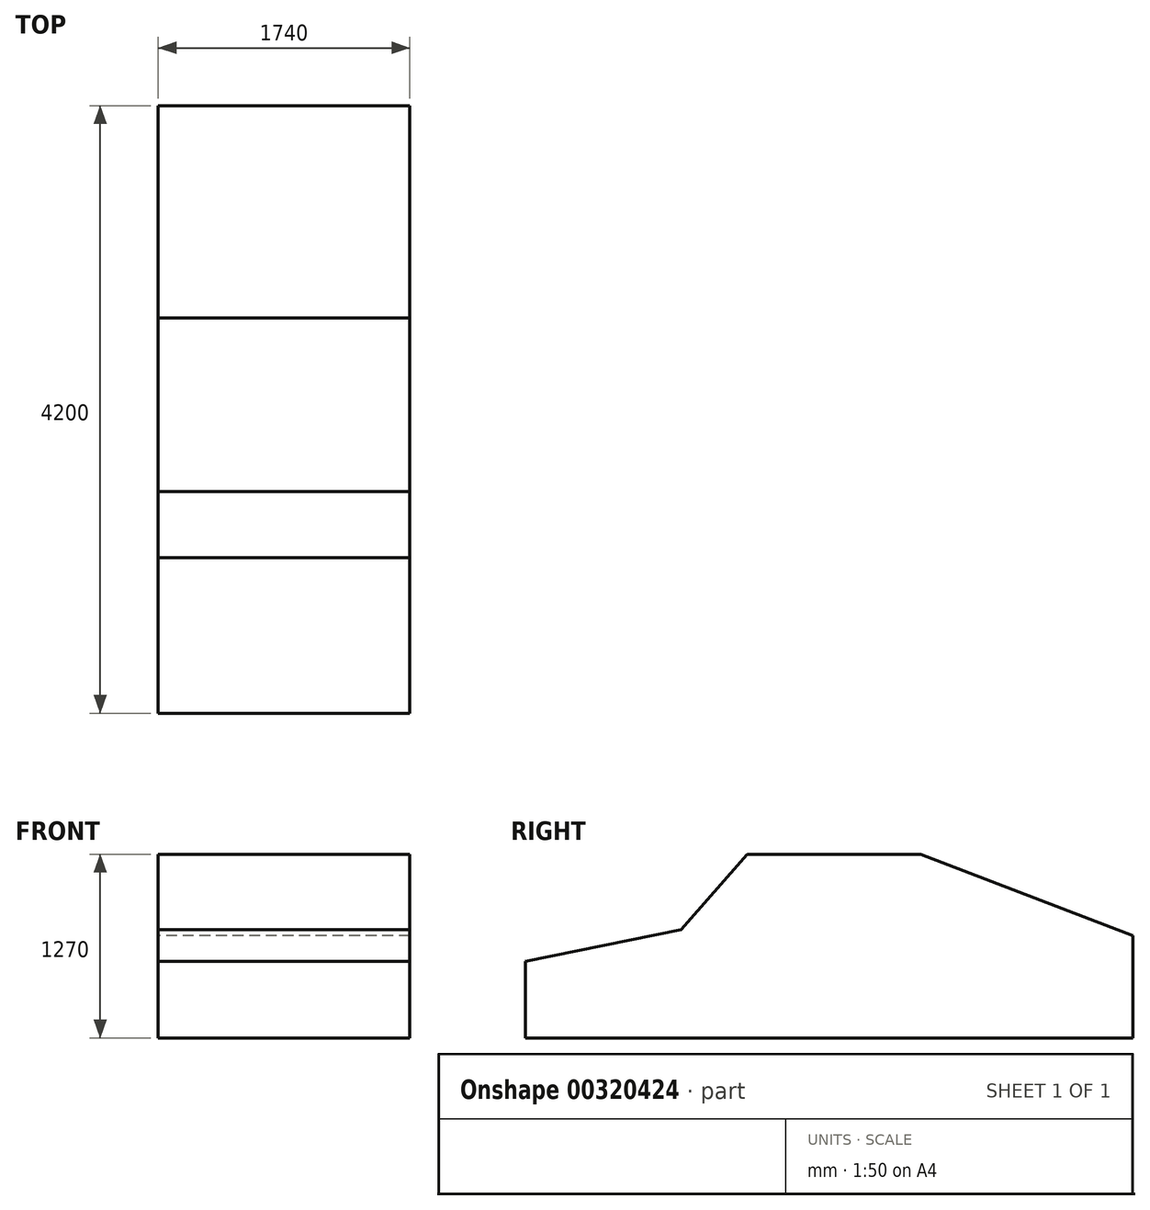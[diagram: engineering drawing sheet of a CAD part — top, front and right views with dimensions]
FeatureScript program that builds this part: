
annotation { "Feature Type Name" : "Feature", "Feature Type Description" : "" }
export const myFeature = defineFeature(function(context is Context, id is Id, definition is map)
    precondition{}
    {
        {
            var Q0;
            Q0=qCreatedBy(makeId("Top.planeOp"),FACE);
            var sketch = newSketch(context, id + "F0", { "sketchPlane" : qUnion([Q0])});
            skLineSegment(sketch, "E0.bottom", {"start": v(-835.88, 2744.57) * mm, "end": v(904.12, 2744.57) * mm});
            skLineSegment(sketch, "E0.top", {"start": v(-835.88, -1455.43) * mm, "end": v(904.12, -1455.43) * mm});
            skLineSegment(sketch, "E0.left", {"start": v(-835.88, 2744.57) * mm, "end": v(-835.88, -1455.43) * mm});
            skLineSegment(sketch, "E0.right", {"start": v(904.12, 2744.57) * mm, "end": v(904.12, -1455.43) * mm});
            skSolve(sketch);
        }
        {
            var Q0;
            Q0 = qSketchRegion(id + "F0", true);
            extrude(context, id + "F1", {"entities" : qUnion([Q0]), "depth" : 1270 * mm});
        }
        {
            var Q0;
            Q0=makeQuery(id+"F1.opExtrude","SWEPT_FACE",FACE,{"disambiguationData":[OSD([sQuery(id+"F0.wireOp",EDGE,"E0.left")])]});
            var sketch = newSketch(context, id + "F2", { "sketchPlane" : qUnion([Q0])});
            skLineSegment(sketch, "E1", {"start": v(1455.43, 529.7) * mm, "end": v(380.81, 746.65) * mm});
            skLineSegment(sketch, "E2", {"start": v(380.81, 746.65) * mm, "end": v(-76.8, 1270) * mm});
            skLineSegment(sketch, "E3", {"start": v(-1276.75, 1270) * mm, "end": v(-2744.57, 705.97) * mm});
            skSolve(sketch);
        }
        {
            var Q0;
            {var subQ0=sQuery(id+"F2.wireOp",EDGE,"E3");Q0=makeQuery(id+"F2.imprint","IMPRINT",FACE,{"disambiguationData":[TD([[makeQuery(id+"F2.imprint","IMPRINT",EDGE,{"derivedFrom":subQ0}),-1.0]])]});}
            var Q1;
            {var subQ0=sQuery(id+"F2.wireOp",EDGE,"E1");Q1=makeQuery(id+"F2.imprint","IMPRINT",FACE,{"disambiguationData":[TD([[makeQuery(id+"F2.imprint","IMPRINT",EDGE,{"derivedFrom":subQ0}),-1.0]])]});}
            var Q2;
            Q2=makeQuery(id+"F1.opExtrude","SWEPT_FACE",FACE,{"disambiguationData":[OSD([sQuery(id+"F0.wireOp",EDGE,"E0.right")])]});
            extrude(context, id + "F3", {"entities" : qUnion([Q0, Q1]), "operationType" : NewBodyOperationType.REMOVE, "endBound" : BoundingType.UP_TO_SURFACE, "oppositeDirection" : true, "endBoundEntityFace" : qUnion([Q2]), "offsetDistance" : 25 * mm, "depth" : 25 * mm});
        }
    });
